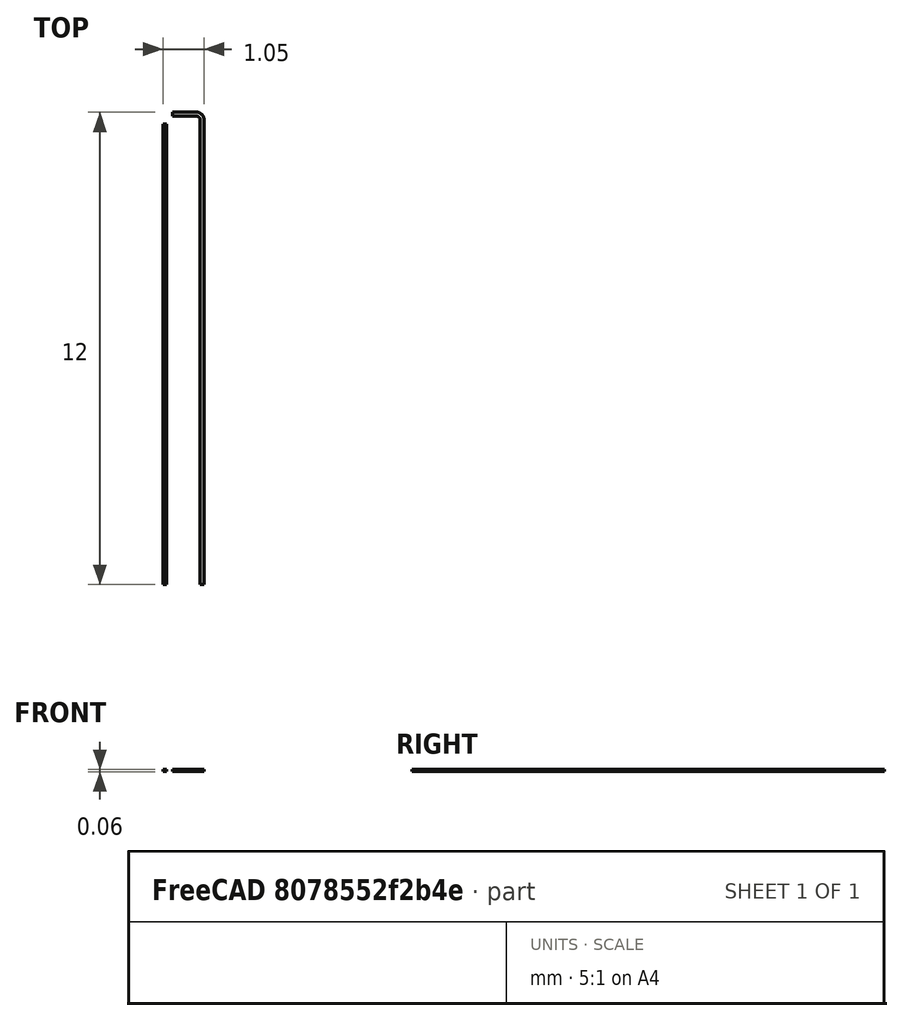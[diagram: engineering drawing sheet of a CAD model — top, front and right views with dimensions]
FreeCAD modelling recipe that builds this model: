
FCSTD DOCUMENT  (FreeCAD 0.16R6712 (Git))
Label: minuswires
License: All rights reserved
LicenseURL: http://en.wikipedia.org/wiki/All_rights_reserved
objects: Sketcher::SketchObject×2, PartDesign::Pad×2, PartDesign::Fillet×2, Part::Fuse×1, Mesh::Feature×1
note: 9 computed .brp shape members not serialized (recipe doc carries the construction recipe); baked Part::Feature solids carry a one-line shape summary decoded from their .brp

FEATURE [Sketcher::SketchObject] Sketch
  sketch-geometry (6):
    g0: LineSegment StartX=0.7 StartY=12 StartZ=0 EndX=1.5 EndY=12 EndZ=0
    g1: LineSegment StartX=1.5 StartY=12 StartZ=0 EndX=1.5 EndY=0 EndZ=0
    g2: LineSegment StartX=1.5 StartY=0 StartZ=0 EndX=1.4 EndY=0 EndZ=0
    g3: LineSegment StartX=1.4 StartY=0 StartZ=0 EndX=1.4 EndY=11.9 EndZ=0
    g4: LineSegment StartX=1.4 StartY=11.9 StartZ=0 EndX=0.7 EndY=11.9 EndZ=0
    g5: LineSegment StartX=0.7 StartY=12 StartZ=0 EndX=0.7 EndY=11.9 EndZ=0
  constraints (18):
    c: Horizontal(g0)
    c: Coincident(g1,g0)
    c: PointOnObject(g1,g-1)
    c: Vertical(g1)
    c: Coincident(g2,g1)
    c: PointOnObject(g2,g-1)
    c: Coincident(g3,g2)
    c: Vertical(g3)
    c: Coincident(g5,g0)
    c: Coincident(g5,g4)
    c: DistanceX(g-2,g0) = 1.5
    c: Coincident(g4,g3)
    c: DistanceX(g3,g0) = 0.1
    c: Horizontal(g4)
    c: DistanceX(g-2,g0) = 0.7
    c: Vertical(g5)
    c: Distance(g4,g0) = 0.1
    c: Distance(g-1,g0) = 12
FEATURE [PartDesign::Pad] Pad
  Length = 0.05
  Length2 = 100
  Midplane = true
  Sketch = -> Sketch
  Type = 0
FEATURE [Sketcher::SketchObject] Sketch001
  sketch-geometry (4):
    g0: LineSegment StartX=0.45 StartY=11.7 StartZ=0 EndX=0.55 EndY=11.7 EndZ=0
    g1: LineSegment StartX=0.55 StartY=11.7 StartZ=0 EndX=0.55 EndY=0 EndZ=0
    g2: LineSegment StartX=0.55 StartY=0 StartZ=0 EndX=0.45 EndY=0 EndZ=0
    g3: LineSegment StartX=0.45 StartY=0 StartZ=0 EndX=0.45 EndY=11.7 EndZ=0
  constraints (12):
    c: Coincident(g0,g1)
    c: Coincident(g1,g2)
    c: Coincident(g2,g3)
    c: Coincident(g3,g0)
    c: Horizontal(g0)
    c: Horizontal(g2)
    c: Vertical(g1)
    c: Vertical(g3)
    c: PointOnObject(g-1,g2)
    c: DistanceX(g2,g1) = 0.1
    c: Distance(g-1,g0) = 11.7
    c: DistanceX(g-2,g2) = 0.45
FEATURE [PartDesign::Pad] Pad001
  Length = 0.05
  Length2 = 100
  Midplane = true
  Sketch = -> Sketch001
  Type = 0
FEATURE [Part::Fuse] Fusion
  Base = -> Pad
  Tool = -> Pad001
FEATURE [PartDesign::Fillet] Fillet
  Base = -> Fusion [Edge11]
  Radius = 0.1
FEATURE [PartDesign::Fillet] Fillet001
  Base = -> Fillet [Edge20]
  Radius = 0.2
FEATURE [Mesh::Feature] Mesh  label="Fillet001 (Meshed)"
